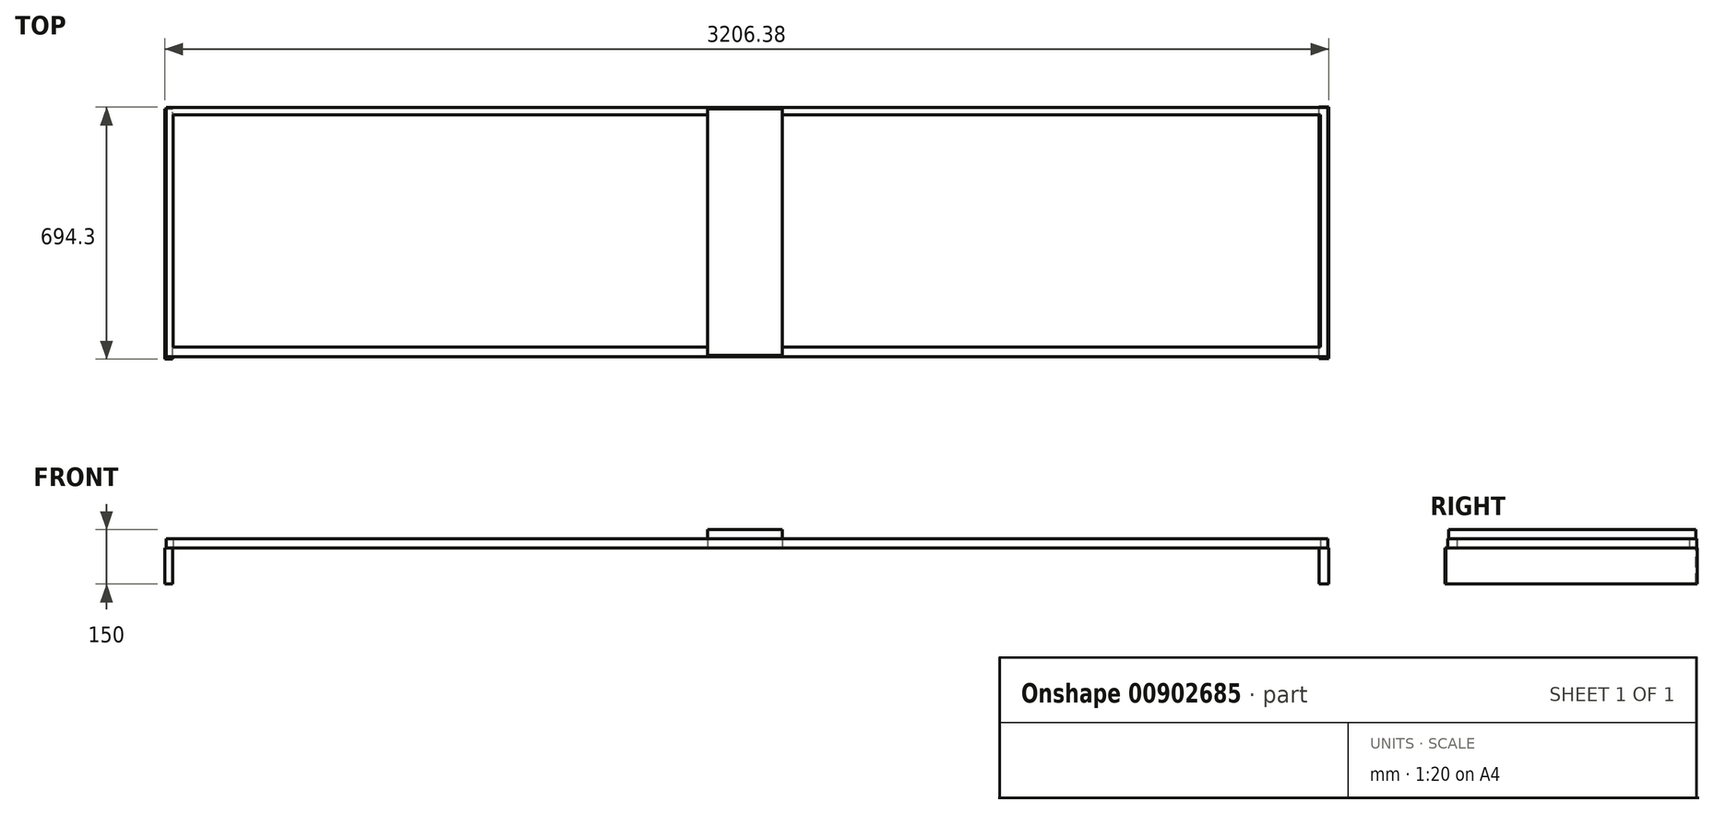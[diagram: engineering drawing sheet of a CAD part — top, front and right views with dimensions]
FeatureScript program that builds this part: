
annotation { "Feature Type Name" : "Feature", "Feature Type Description" : "" }
export const myFeature = defineFeature(function(context is Context, id is Id, definition is map)
    precondition{}
    {
        {
            var Q0;
            Q0=qCreatedBy(makeId("Top.planeOp"),FACE);
            var sketch = newSketch(context, id + "F0", { "sketchPlane" : qUnion([Q0])});
            skLineSegment(sketch, "E0.bottom", {"start": v(-171.07, -35.54) * mm, "end": v(3028.93, -35.54) * mm});
            skLineSegment(sketch, "E0.top", {"start": v(-171.07, -55.54) * mm, "end": v(3028.93, -55.54) * mm});
            skLineSegment(sketch, "E0.left", {"start": v(-171.07, -35.54) * mm, "end": v(-171.07, -55.54) * mm});
            skLineSegment(sketch, "E0.right", {"start": v(3028.93, -35.54) * mm, "end": v(3028.93, -55.54) * mm});
            skLineSegment(sketch, "E1.bottom", {"start": v(-171.07, -55.54) * mm, "end": v(-151.07, -55.54) * mm});
            skLineSegment(sketch, "E1.top", {"start": v(-171.07, -695.54) * mm, "end": v(-151.07, -695.54) * mm});
            skLineSegment(sketch, "E1.left", {"start": v(-171.07, -55.54) * mm, "end": v(-171.07, -695.54) * mm});
            skLineSegment(sketch, "E1.right", {"start": v(-151.07, -55.54) * mm, "end": v(-151.07, -695.54) * mm});
            skLineSegment(sketch, "E2.bottom", {"start": v(3008.93, -55.54) * mm, "end": v(3028.93, -55.54) * mm});
            skLineSegment(sketch, "E2.top", {"start": v(3008.93, -695.54) * mm, "end": v(3028.93, -695.54) * mm});
            skLineSegment(sketch, "E2.left", {"start": v(3008.93, -55.54) * mm, "end": v(3008.93, -695.54) * mm});
            skLineSegment(sketch, "E2.right", {"start": v(3028.93, -55.54) * mm, "end": v(3028.93, -695.54) * mm});
            skLineSegment(sketch, "E3.bottom", {"start": v(-171.07, -695.54) * mm, "end": v(3028.93, -695.54) * mm});
            skLineSegment(sketch, "E3.top", {"start": v(-171.07, -721.9) * mm, "end": v(3028.93, -721.9) * mm});
            skLineSegment(sketch, "E3.left", {"start": v(-171.07, -695.54) * mm, "end": v(-171.07, -721.9) * mm});
            skLineSegment(sketch, "E3.right", {"start": v(3028.93, -695.54) * mm, "end": v(3028.93, -721.9) * mm});
            skSolve(sketch);
        }
        {
            var Q0;
            Q0 = qSketchRegion(id + "F0", true);
            extrude(context, id + "F1", {"entities" : qUnion([Q0]), "depth" : 25 * mm, "offsetDistance" : 25 * mm});
        }
        {
            var Q0;
            Q0=qCreatedBy(makeId("Top.planeOp"),FACE);
            var sketch = newSketch(context, id + "F2", { "sketchPlane" : qUnion([Q0])});
            skLineSegment(sketch, "E4.bottom", {"start": v(1320.99, -38.41) * mm, "end": v(1526.06, -38.41) * mm});
            skLineSegment(sketch, "E4.top", {"start": v(1320.99, -718.41) * mm, "end": v(1526.06, -718.41) * mm});
            skLineSegment(sketch, "E4.left", {"start": v(1320.99, -38.41) * mm, "end": v(1320.99, -718.41) * mm});
            skLineSegment(sketch, "E4.right", {"start": v(1526.06, -38.41) * mm, "end": v(1526.06, -718.41) * mm});
            skPoint(sketch, "E5", {"position": v(1320.99, -38.41) * mm});
            skSolve(sketch);
        }
        {
            var Q0;
            Q0 = qSketchRegion(id + "F2", true);
            extrude(context, id + "F3", {"entities" : qUnion([Q0]), "operationType" : NewBodyOperationType.ADD, "depth" : 50 * mm, "offsetDistance" : 25 * mm});
        }
        {
            var Q0;
            Q0=qCreatedBy(makeId("Top.planeOp"),FACE);
            var sketch = newSketch(context, id + "F4", { "sketchPlane" : qUnion([Q0])});
            skLineSegment(sketch, "E6.bottom", {"start": v(-174.87, -728.82) * mm, "end": v(-152.93, -728.82) * mm});
            skLineSegment(sketch, "E6.top", {"start": v(-174.87, -38.78) * mm, "end": v(-152.93, -38.78) * mm});
            skLineSegment(sketch, "E6.left", {"start": v(-174.87, -728.82) * mm, "end": v(-174.87, -38.78) * mm});
            skLineSegment(sketch, "E6.right", {"start": v(-152.93, -728.82) * mm, "end": v(-152.93, -38.78) * mm});
            skLineSegment(sketch, "E7.bottom", {"start": v(3004.7, -727) * mm, "end": v(3031.51, -727) * mm});
            skLineSegment(sketch, "E7.top", {"start": v(3004.7, -34.52) * mm, "end": v(3031.51, -34.52) * mm});
            skLineSegment(sketch, "E7.left", {"start": v(3004.7, -727) * mm, "end": v(3004.7, -34.52) * mm});
            skLineSegment(sketch, "E7.right", {"start": v(3031.51, -727) * mm, "end": v(3031.51, -34.52) * mm});
            skSolve(sketch);
        }
        {
            var Q0;
            Q0 = qSketchRegion(id + "F4", true);
            extrude(context, id + "F5", {"entities" : qUnion([Q0]), "operationType" : NewBodyOperationType.ADD, "depth" : -100 * mm, "offsetDistance" : 25 * mm});
        }
        {
            var Q0;
            Q0 = qSketchRegion(id + "F4", true);
            extrude(context, id + "F6", {"entities" : qUnion([Q0]), "operationType" : NewBodyOperationType.ADD, "depth" : -100 * mm, "offsetDistance" : 25 * mm});
        }
    });
